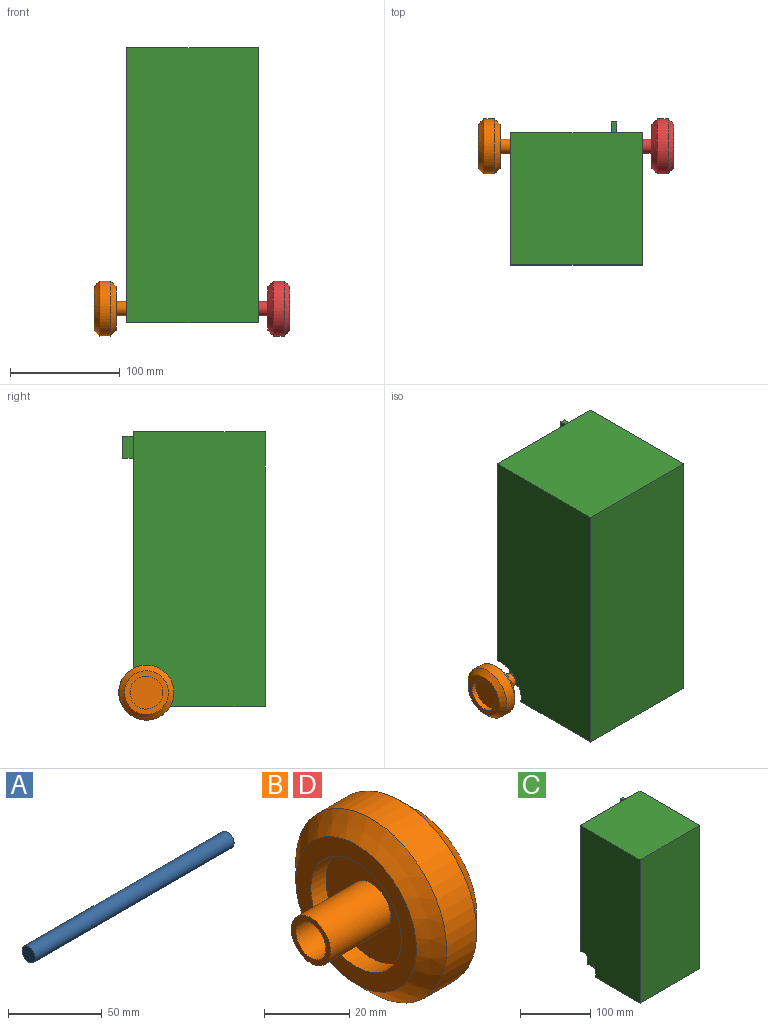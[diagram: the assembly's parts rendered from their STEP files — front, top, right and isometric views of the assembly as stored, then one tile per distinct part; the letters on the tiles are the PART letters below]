
ASSEMBLY  parts=4 mates=2
PART A: 3 faces, bbox 150x10x10 mm
  f0: cylinder r=5mm len=150mm, axis (-1,0,0), area 4712.4mm2, adj f1,f2
  f1: plane 10x10mm, normal (1,0,0), area 78.5mm2, adj f0
  f2: plane 10x10mm, normal (-1,0,0), area 78.5mm2, adj f0
PART B: 22 faces, bbox 35x50x50 mm
  f0: cylinder r=25mm len=50mm, axis (-1,0,0), area 1570.8mm2, adj f3,f4
  f1: plane 40x40mm, normal (1,0,0), area 549.8mm2, adj f3,f7
  f2: plane 40x40mm, normal (-1,0,0), area 549.8mm2, adj f4,f5
  f3: cone r=20mm half-angle=45deg, axis (-1,0,0), area 999.6mm2, adj f0,f1
  f4: cone r=25mm half-angle=45deg, axis (1,0,0), area 999.6mm2, adj f0,f2
  f5: cylinder r=15mm len=30mm, axis (-1,0,0), area 471.2mm2, adj f2,f6
  f6: plane 30x30mm, normal (-1,0,0), area 574.1mm2, adj f5,f10
  f7: cylinder r=15mm len=30mm, axis (1,0,0), area 471.2mm2, adj f1,f8
  f8: plane 30x30mm, normal (1,0,0), area 706.9mm2, adj f7
  f9: cylinder r=5mm len=20mm, axis (1,0,0), area 628.3mm2, adj f11,f12
  f10: cylinder r=6.5mm len=20mm, axis (1,0,0), area 816.8mm2, adj f6,f11
  f11: plane 13x13mm, normal (-1,0,0), area 54.2mm2, adj f9,f10
  f12: plane 10x10mm, normal (-1,0,0), area 78.5mm2, adj f9
  f13: cylinder r=22.5mm len=45mm, axis (-1,0,0), area 1120.9mm2, adj f16,f17
  f14: plane 37.93x37.93mm, normal (-1,0,0), area 167.8mm2, adj f16,f20
  f15: plane 37.93x37.93mm, normal (1,0,0), area 167.8mm2, adj f17,f18
  f16: cone r=18.23mm half-angle=45deg, axis (-1,0,0), area 651.3mm2, adj f13,f14
  f17: cone r=23.23mm half-angle=45deg, axis (1,0,0), area 651.3mm2, adj f13,f15
  f18: cylinder r=17.5mm len=35mm, axis (-1,0,0), area 549.8mm2, adj f15,f19
  f19: plane 35x35mm, normal (1,0,0), area 962.1mm2, adj f18
  f20: cylinder r=17.5mm len=35mm, axis (1,0,0), area 549.8mm2, adj f14,f21
  f21: plane 35x35mm, normal (-1,0,0), area 962.1mm2, adj f20
PART C: 16 faces, bbox 120x130x250 mm
  f0: plane 250x120mm, normal (0,1,0), area 28997.1mm2, adj f1,f2,f4,f5,f6,f7,f8,f9
  f1: plane 250x120mm, normal (-1,0,0), area 29199.7mm2, adj f0,f2,f3,f5,f6
  f2: plane 120x120mm, normal (0,0,-1), area 13493.9mm2, adj f0,f1,f3,f4,f6,f7,f8,f9
  f3: plane 250x120mm, normal (0,-1,0), area 30000mm2, adj f1,f2,f4,f5
  f4: plane 250x120mm, normal (1,0,0), area 29227mm2, adj f0,f2,f3,f5,f8
  f5: plane 120x120mm, normal (0,0,1), area 14400mm2, adj f0,f1,f3,f4
  f6: cylinder r=26mm len=31.01mm, axis (-1,0,0), area 756.5mm2, adj f0,f1,f2,f7
  f7: plane 31.01x30.53mm, normal (-1,0,0), area 721.7mm2, adj f0,f2,f6,f10
  f8: cylinder r=26mm len=30.67mm, axis (1,0,0), area 742.8mm2, adj f0,f2,f4,f9
  f9: plane 30.67x29.97mm, normal (1,0,0), area 694.4mm2, adj f0,f2,f8,f10
  f10: cylinder r=5mm len=90mm, axis (1,0,0), area 2827.4mm2, adj f7,f9
  f11: plane 20.27x10mm, normal (-1,0,0), area 202.7mm2, adj f0,f12,f14,f15
  f12: plane 10x5.02mm, normal (0.09,0,1), area 50.3mm2, adj f0,f11,f13,f15
  f13: plane 19.83x10mm, normal (1,0,0), area 198.3mm2, adj f0,f12,f14,f15
  f14: plane 10x5.02mm, normal (0,0,-1), area 50.2mm2, adj f0,f11,f13,f15
  f15: plane 20.27x5.02mm, normal (0,1,0), area 100.6mm2, adj f11,f12,f13,f14
PART D: same geometry as B
PLACE A t=(1.6,130.33,98.37)mm
PLACE B rot(axis=(0,1,0),180deg) t=(-0.7,130.11,98.38)mm
PLACE C t=(105.36,40.25,85.61)mm
PLACE D t=(137.37,130.33,98.37)mm
MATE cylindrical D.f0 <-> A.f0  axis (-1,0,0) through (122.37,130.33,98.37)mm
MATE cylindrical B.f0 <-> C.f10  axis (1,0,0) through (14.3,130.11,98.38)mm
